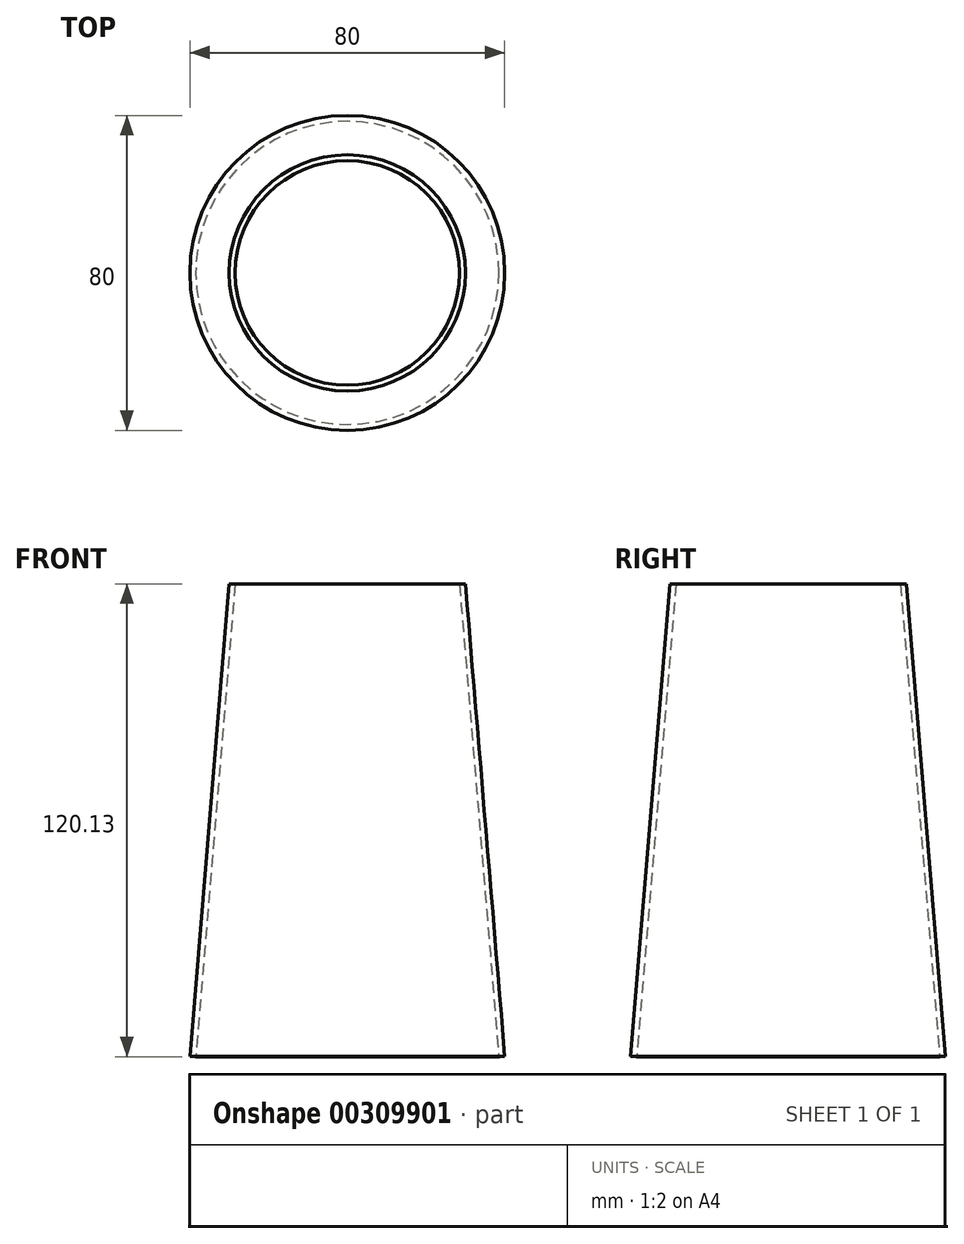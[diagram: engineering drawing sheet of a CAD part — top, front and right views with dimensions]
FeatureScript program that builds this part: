
annotation { "Feature Type Name" : "Feature", "Feature Type Description" : "" }
export const myFeature = defineFeature(function(context is Context, id is Id, definition is map)
    precondition{}
    {
        {
            var Q0;
            Q0=qCreatedBy(makeId("Front.planeOp"),FACE);
            var sketch = newSketch(context, id + "F0", { "sketchPlane" : qUnion([Q0])});
            skLineSegment(sketch, "E0", {"start": v(40, -0.92) * mm, "end": v(30, 119.08) * mm});
            skPoint(sketch, "E1.endSnap0", {"position": v(0, 120) * mm});
            skLineSegment(sketch, "E2", {"start": v(0, 120) * mm, "end": v(0, 0) * mm});
            skLineSegment(sketch, "E3.0", {"start": v(38.5, -1.05) * mm, "end": v(28.5, 118.95) * mm});
            skLineSegment(sketch, "E4", {"start": v(28.5, 118.95) * mm, "end": v(30, 119.08) * mm});
            skLineSegment(sketch, "E5", {"start": v(38.5, -1.05) * mm, "end": v(40, -0.92) * mm});
            skFitSpline(sketch, "E6", {"points": [v(-253.55, 85.72) * mm, v(-263.96, 83.24) * mm, v(-272.53, 83.22) * mm, v(-297.66, 83.15) * mm, v(-344.85, 87.3) * mm, v(-373.65, 89.68) * mm], "startDerivative": vector(-78.36, -22.87) * mm, "endDerivative": vector(-115.31, 8.25) * mm});
            skFitSpline(sketch, "E7", {"points": [v(-256.71, 36.74) * mm, v(-261.06, 38.66) * mm, v(-266.18, 39.8) * mm, v(-270.43, 40.66) * mm, v(-296.57, 39.05) * mm, v(-322.55, 35.87) * mm, v(-349.78, 29.6) * mm, v(-373.65, 21.4) * mm], "startDerivative": vector(-50.82, 26.63) * mm, "endDerivative": vector(-127.45, -26.2) * mm});
            skLineSegment(sketch, "E8", {"start": v(-253.55, 85.72) * mm, "end": v(-236.18, 80.23) * mm});
            skLineSegment(sketch, "E9", {"start": v(-236.18, 80.23) * mm, "end": v(-236.18, 47.74) * mm});
            skLineSegment(sketch, "E10", {"start": v(-236.18, 47.74) * mm, "end": v(-256.71, 36.74) * mm});
            skLineSegment(sketch, "E11", {"start": v(-373.65, 21.4) * mm, "end": v(-373.65, 89.68) * mm});
            skLineSegment(sketch, "E12", {"start": v(-373.65, 89.68) * mm, "end": v(-373.65, 91.18) * mm});
            skLineSegment(sketch, "E13", {"start": v(-373.65, 21.4) * mm, "end": v(-373.65, 19.9) * mm});
            skArc(sketch, "E14", {"start": v(-256.71, 36.74) * mm, "mid": v(-316.1, 34.63) * mm, "end": v(-373.65, 19.9) * mm});
            skArc(sketch, "E15", {"start": v(-373.65, 91.18) * mm, "mid": v(-313.7, 86.26) * mm, "end": v(-253.55, 85.72) * mm});
            skLineSegment(sketch, "E16", {"start": v(-368.65, 116.1) * mm, "end": v(-368.65, 0) * mm});
            skLineSegment(sketch, "E17.bottom", {"start": v(-373.65, 116.1) * mm, "end": v(-236.18, 116.1) * mm});
            skLineSegment(sketch, "E17.top", {"start": v(-373.65, 0) * mm, "end": v(-236.18, 0) * mm});
            skLineSegment(sketch, "E17.left", {"start": v(-373.65, 116.1) * mm, "end": v(-373.65, 0) * mm});
            skLineSegment(sketch, "E17.right", {"start": v(-236.18, 116.1) * mm, "end": v(-236.18, 0) * mm});
            skLineSegment(sketch, "E18.0", {"start": v(-363.65, 116.1) * mm, "end": v(-363.65, 0) * mm});
            skLineSegment(sketch, "E19.0", {"start": v(-358.65, 116.1) * mm, "end": v(-358.65, 0) * mm});
            skLineSegment(sketch, "E20.0", {"start": v(-353.65, 116.1) * mm, "end": v(-353.65, 0) * mm});
            skLineSegment(sketch, "E21", {"start": v(-348.65, 116.1) * mm, "end": v(-348.65, 0) * mm});
            skLineSegment(sketch, "E22.0", {"start": v(-343.65, 164.08) * mm, "end": v(-343.65, 47.97) * mm});
            skLineSegment(sketch, "E23.0", {"start": v(-338.65, 164.08) * mm, "end": v(-338.65, 47.97) * mm});
            skLineSegment(sketch, "E24.0", {"start": v(-333.65, 164.08) * mm, "end": v(-333.65, 47.97) * mm});
            skSolve(sketch);
        }
        {
            var Q0;
            Q0=makeQuery(id+"F0.imprint","IMPRINT",FACE,{"disambiguationData":[TD([[makeQuery(id+"F0.imprint","IMPRINT",EDGE,{"derivedFrom":sQuery(id+"F0.wireOp",EDGE,"E0")}),1.0]])]});
            var Q1;
            Q1=sQuery(id+"F0.wireOp",EDGE,"E2");
            revolve(context, id + "F1", {"entities" : qUnion([Q0]), "axis" : qUnion([Q1]), "revolveType" : RevolveType.FULL});
        }
    });
